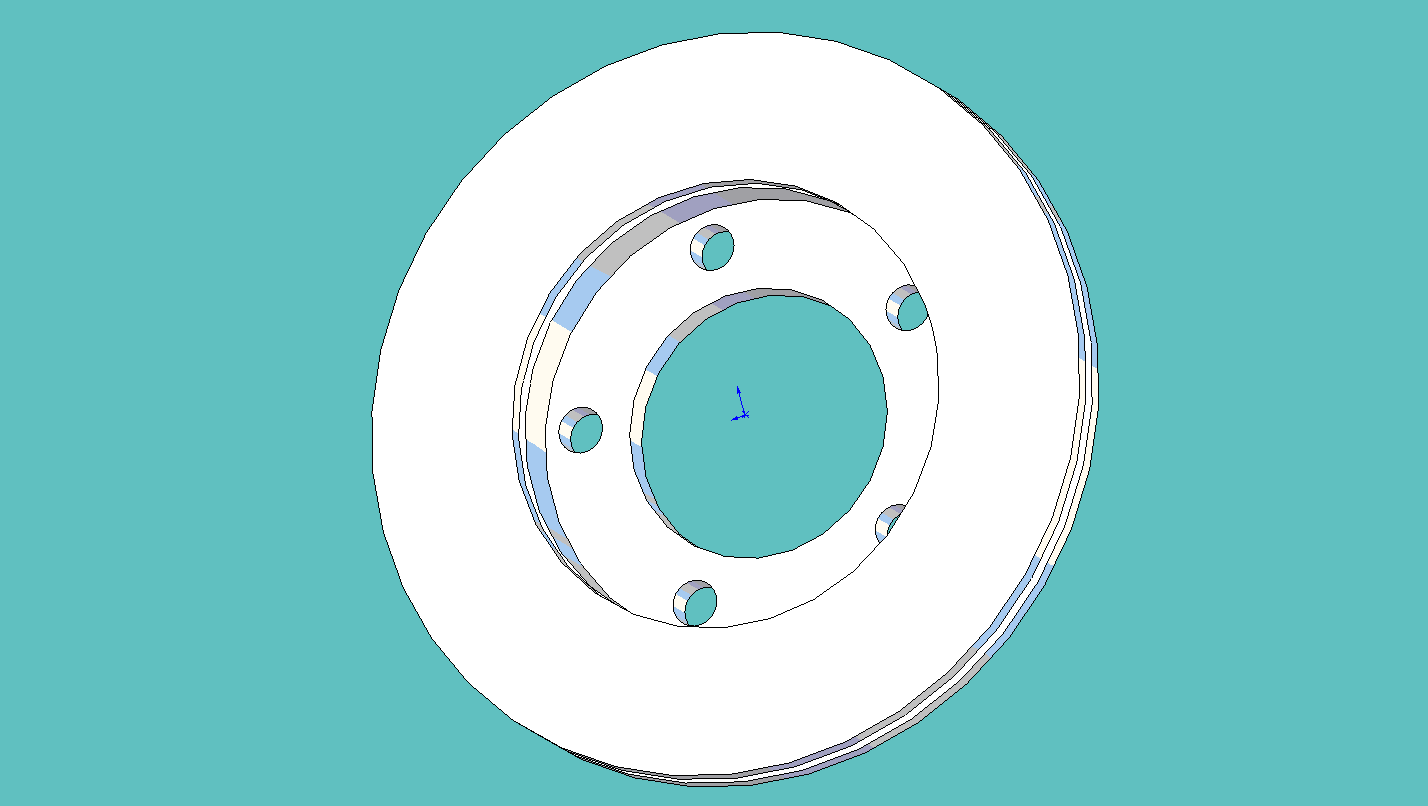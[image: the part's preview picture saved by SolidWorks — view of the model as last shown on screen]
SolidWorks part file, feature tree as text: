
SOLIDWORKS PART (.sldprt)
format: sldprt  version: not decoded by parser v0  size: 670,208 bytes
history: native  units: mm
features: sketch x5, extrude x4, material x1, chamfer x1, cut_extrude x1, plane x1 (+13 scaffold rows collapsed)
feature tree (26):
  scaffold x13  (default folders/planes/origin — collapsed)
  material  "Material <not specified>"
  sketch  "Sketch1"  dims[D1=279.4mm D2=177.8mm D3=~94.511865mm]
  extrude  "Extrude4"  Depth=6.35mm
  extrude  "Extrude5"  [1 undecoded]
  sketch  "Sketch1<9>"  dims[D1=25.4mm]
  chamfer  "Chamfer1"  Distance=3mm Angle=45deg
  sketch  "Sketch2"
  cut_extrude  "Cut-Extrude1"  Depth=20mm
  sketch  "Sketch3"
  extrude  "Extrude6"  Depth=6.35mm
  plane  "Plane1"  Offset=6.35mm
  sketch  "Sketch4"
  extrude  "Extrude7"  Depth=6.35mm
decode coverage: 7 of 11 modeling features carry decoded parameters
note: ~ marks probable driven/reference dimensions
note: 1 parameter value undecoded
note: suppression state not decoded; provenance and decode notes live in map.json
